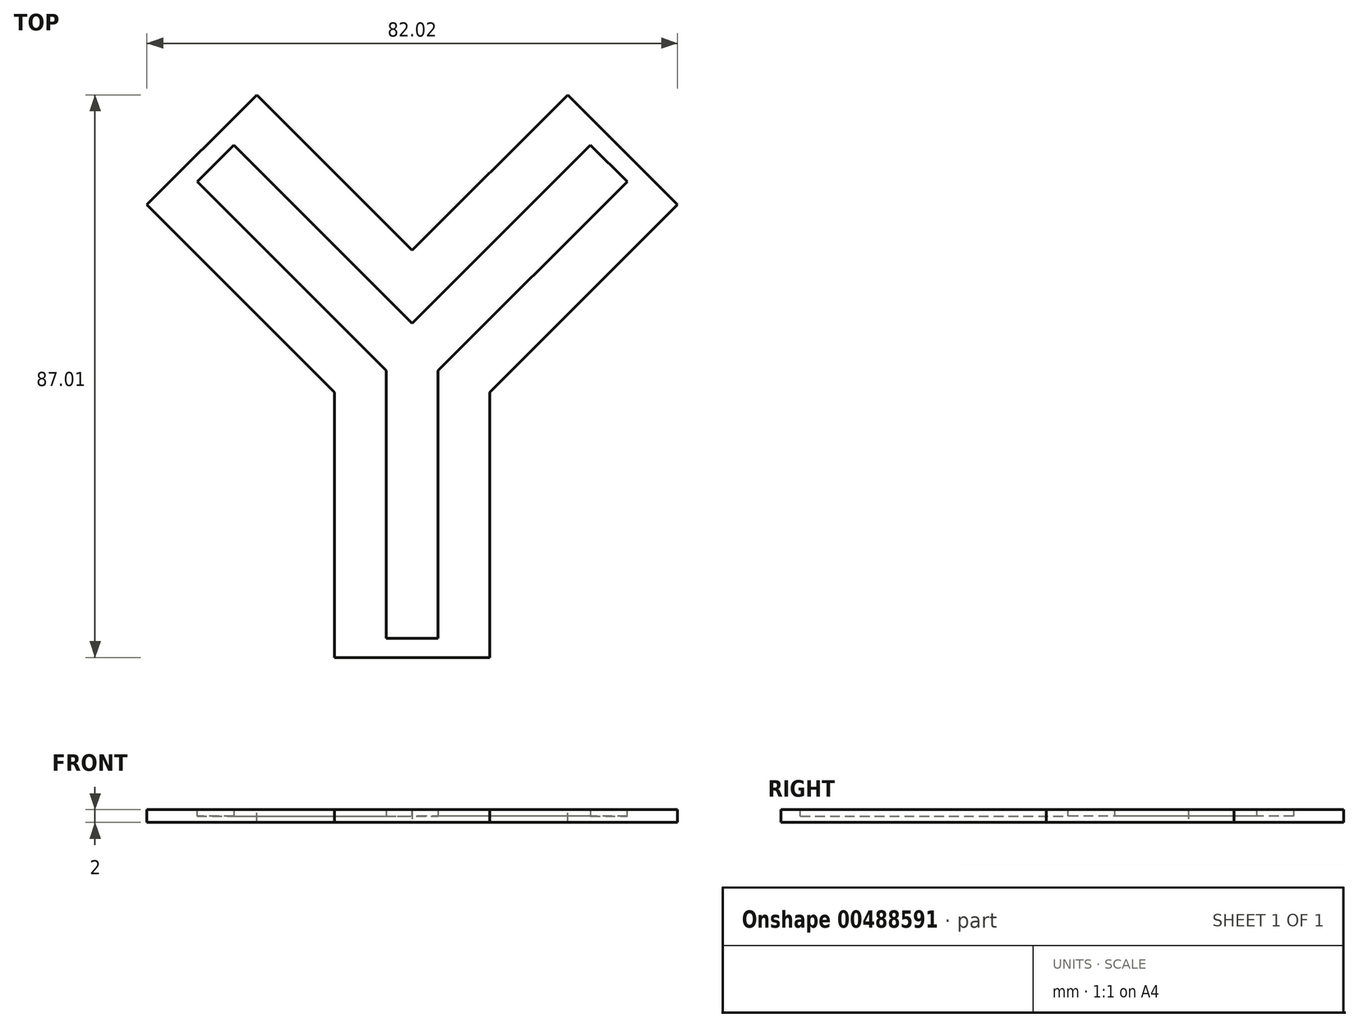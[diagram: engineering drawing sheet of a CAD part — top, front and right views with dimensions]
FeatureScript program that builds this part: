
annotation { "Feature Type Name" : "Feature", "Feature Type Description" : "" }
export const myFeature = defineFeature(function(context is Context, id is Id, definition is map)
    precondition{}
    {
        {
            var Q0;
            Q0=qCreatedBy(makeId("Front.planeOp"),FACE);
            var sketch = newSketch(context, id + "F0", { "sketchPlane" : qUnion([Q0])});
            skLineSegment(sketch, "E0", {"start": v(0, 0) * mm, "end": v(4, 0) * mm});
            skLineSegment(sketch, "E1", {"start": v(4, 0) * mm, "end": v(4, 1) * mm});
            skLineSegment(sketch, "E2", {"start": v(4, 1) * mm, "end": v(12, 1) * mm});
            skLineSegment(sketch, "E3", {"start": v(12, 1) * mm, "end": v(12, -1) * mm});
            skLineSegment(sketch, "E4", {"start": v(12, -1) * mm, "end": v(-12, -1) * mm});
            skLineSegment(sketch, "E5", {"start": v(-12, -1) * mm, "end": v(-12, 1) * mm});
            skLineSegment(sketch, "E6", {"start": v(-12, 1) * mm, "end": v(-4, 1) * mm});
            skLineSegment(sketch, "E7", {"start": v(-4, 1) * mm, "end": v(-4, 0) * mm});
            skLineSegment(sketch, "E8", {"start": v(-4, 0) * mm, "end": v(0, 0) * mm});
            skSolve(sketch);
        }
        {
            var Q0;
            Q0 = qSketchRegion(id + "F0", true);
            extrude(context, id + "F1", {"entities" : qUnion([Q0]), "depth" : 43 * mm});
        }
        {
            var Q0;
            Q0=qCreatedBy(makeId("Front.planeOp"),FACE);
            var sketch = newSketch(context, id + "F2", { "sketchPlane" : qUnion([Q0])});
            skLineSegment(sketch, "E9", {"start": v(0, 0) * mm, "end": v(0, 49.54) * mm});
            skSolve(sketch);
        }
        {
            var Q0;
            Q0=qCreatedBy(makeId("Front.planeOp"),FACE);
            var Q1;
            Q1 = qBodyType(qCreatedBy(id + "F2" ,EDGE), BodyType.WIRE);
            cPlane(context, id + "F3", {"entities" : qUnion([Q0, Q1]), "cplaneType" : CPlaneType.LINE_ANGLE, "offset" : 25 * mm, "angle" : 45 * degree, "width" : 150 * mm, "height" : 150 * mm});
        }
        {
            var Q0;
            Q0=qCreatedBy(id+"F3.planeOp",FACE);
            var Q1;
            Q1 = qBodyType(qCreatedBy(id + "F2" ,EDGE), BodyType.WIRE);
            cPlane(context, id + "F4", {"entities" : qUnion([Q0, Q1]), "cplaneType" : CPlaneType.LINE_ANGLE, "offset" : 25 * mm, "angle" : 90 * degree, "width" : 150 * mm, "height" : 150 * mm});
        }
        {
            var Q0;
            Q0=qCreatedBy(id+"F3.planeOp",FACE);
            var sketch = newSketch(context, id + "F5", { "sketchPlane" : qUnion([Q0])});
            skLineSegment(sketch, "E10", {"start": v(0, 0) * mm, "end": v(4, 0) * mm});
            skLineSegment(sketch, "E11", {"start": v(4, 0) * mm, "end": v(4, 1) * mm});
            skLineSegment(sketch, "E12", {"start": v(4, 1) * mm, "end": v(12, 1) * mm});
            skLineSegment(sketch, "E13", {"start": v(12, 1) * mm, "end": v(12, -1) * mm});
            skLineSegment(sketch, "E14", {"start": v(12, -1) * mm, "end": v(-12, -1) * mm});
            skLineSegment(sketch, "E15", {"start": v(-12, -1) * mm, "end": v(-12, 1) * mm});
            skLineSegment(sketch, "E16", {"start": v(-12, 1) * mm, "end": v(-4, 1) * mm});
            skLineSegment(sketch, "E17", {"start": v(-4, 1) * mm, "end": v(-4, 0) * mm});
            skLineSegment(sketch, "E18", {"start": v(-4, 0) * mm, "end": v(0, 0) * mm});
            skSolve(sketch);
        }
        {
            var Q0;
            Q0 = qSketchRegion(id + "F5", true);
            extrude(context, id + "F6", {"entities" : qUnion([Q0]), "operationType" : NewBodyOperationType.ADD, "depth" : 43 * mm});
        }
        {
            var Q0;
            Q0=qCreatedBy(id+"F4.planeOp",FACE);
            var sketch = newSketch(context, id + "F7", { "sketchPlane" : qUnion([Q0])});
            skLineSegment(sketch, "E19", {"start": v(0, 0) * mm, "end": v(-4, 0) * mm});
            skLineSegment(sketch, "E20", {"start": v(-4, 0) * mm, "end": v(-4, 1) * mm});
            skLineSegment(sketch, "E21", {"start": v(-4, 1) * mm, "end": v(-12, 1) * mm});
            skLineSegment(sketch, "E22", {"start": v(-12, 1) * mm, "end": v(-12, -1) * mm});
            skLineSegment(sketch, "E23", {"start": v(-12, -1) * mm, "end": v(12, -1) * mm});
            skLineSegment(sketch, "E24", {"start": v(12, -1) * mm, "end": v(12, 1) * mm});
            skLineSegment(sketch, "E25", {"start": v(12, 1) * mm, "end": v(4, 1) * mm});
            skLineSegment(sketch, "E26", {"start": v(4, 1) * mm, "end": v(4, 0) * mm});
            skLineSegment(sketch, "E27", {"start": v(4, 0) * mm, "end": v(0, 0) * mm});
            skSolve(sketch);
        }
        {
            var Q0;
            Q0 = qSketchRegion(id + "F7", true);
            extrude(context, id + "F8", {"entities" : qUnion([Q0]), "operationType" : NewBodyOperationType.ADD, "depth" : 43 * mm});
        }
        {
            var Q0;
            Q0=makeQuery(id+"F1.opExtrude","CAP_FACE",FACE,{"disambiguationData":[OSD([sQuery(id+"F0.wireOp",EDGE,"E0"),sQuery(id+"F0.wireOp",EDGE,"E1"),sQuery(id+"F0.wireOp",EDGE,"E2"),sQuery(id+"F0.wireOp",EDGE,"E3"),sQuery(id+"F0.wireOp",EDGE,"E4"),sQuery(id+"F0.wireOp",EDGE,"E5"),sQuery(id+"F0.wireOp",EDGE,"E6"),sQuery(id+"F0.wireOp",EDGE,"E7"),sQuery(id+"F0.wireOp",EDGE,"E8")])],"isStart":false});
            var sketch = newSketch(context, id + "F9", { "sketchPlane" : qUnion([Q0])});
            skLineSegment(sketch, "E28", {"start": v(0, 0) * mm, "end": v(-4, 0) * mm});
            skLineSegment(sketch, "E29", {"start": v(-4, 0) * mm, "end": v(-4, 1) * mm});
            skLineSegment(sketch, "E30", {"start": v(-4, 1) * mm, "end": v(4, 1) * mm});
            skLineSegment(sketch, "E31", {"start": v(4, 1) * mm, "end": v(4, 0) * mm});
            skLineSegment(sketch, "E32", {"start": v(4, 0) * mm, "end": v(0, 0) * mm});
            skSolve(sketch);
        }
        {
            var Q0;
            Q0 = qSketchRegion(id + "F9", true);
            extrude(context, id + "F10", {"entities" : qUnion([Q0]), "operationType" : NewBodyOperationType.REMOVE, "oppositeDirection" : true, "depth" : 43 * mm});
        }
        {
            var Q0;
            Q0=makeQuery(id+"F6.opExtrude","CAP_FACE",FACE,{"disambiguationData":[OSD([sQuery(id+"F5.wireOp",EDGE,"E10"),sQuery(id+"F5.wireOp",EDGE,"E11"),sQuery(id+"F5.wireOp",EDGE,"E12"),sQuery(id+"F5.wireOp",EDGE,"E13"),sQuery(id+"F5.wireOp",EDGE,"E14"),sQuery(id+"F5.wireOp",EDGE,"E15"),sQuery(id+"F5.wireOp",EDGE,"E16"),sQuery(id+"F5.wireOp",EDGE,"E17"),sQuery(id+"F5.wireOp",EDGE,"E18")])],"isStart":false});
            var sketch = newSketch(context, id + "F11", { "sketchPlane" : qUnion([Q0])});
            skLineSegment(sketch, "E33", {"start": v(0, 0) * mm, "end": v(-4, 0) * mm});
            skLineSegment(sketch, "E34", {"start": v(-4, 0) * mm, "end": v(-4, 1) * mm});
            skLineSegment(sketch, "E35", {"start": v(-4, 1) * mm, "end": v(4, 1) * mm});
            skLineSegment(sketch, "E36", {"start": v(4, 1) * mm, "end": v(4, 0) * mm});
            skLineSegment(sketch, "E37", {"start": v(4, 0) * mm, "end": v(0, 0) * mm});
            skSolve(sketch);
        }
        {
            var Q0;
            Q0 = qSketchRegion(id + "F11", true);
            extrude(context, id + "F12", {"entities" : qUnion([Q0]), "operationType" : NewBodyOperationType.REMOVE, "oppositeDirection" : true, "depth" : 43 * mm});
        }
        {
            var Q0;
            Q0=makeQuery(id+"F8.opExtrude","CAP_FACE",FACE,{"disambiguationData":[OSD([sQuery(id+"F7.wireOp",EDGE,"E19"),sQuery(id+"F7.wireOp",EDGE,"E20"),sQuery(id+"F7.wireOp",EDGE,"E21"),sQuery(id+"F7.wireOp",EDGE,"E22"),sQuery(id+"F7.wireOp",EDGE,"E23"),sQuery(id+"F7.wireOp",EDGE,"E24"),sQuery(id+"F7.wireOp",EDGE,"E25"),sQuery(id+"F7.wireOp",EDGE,"E26"),sQuery(id+"F7.wireOp",EDGE,"E27")])],"isStart":false});
            var sketch = newSketch(context, id + "F13", { "sketchPlane" : qUnion([Q0])});
            skLineSegment(sketch, "E38", {"start": v(0, 0) * mm, "end": v(-4, 0) * mm});
            skLineSegment(sketch, "E39", {"start": v(-4, 0) * mm, "end": v(-4, 1) * mm});
            skLineSegment(sketch, "E40", {"start": v(-4, 1) * mm, "end": v(4, 1) * mm});
            skLineSegment(sketch, "E41", {"start": v(4, 1) * mm, "end": v(4, 0) * mm});
            skLineSegment(sketch, "E42", {"start": v(4, 0) * mm, "end": v(0, 0) * mm});
            skSolve(sketch);
        }
        {
            var Q0;
            Q0 = qSketchRegion(id + "F13", true);
            extrude(context, id + "F14", {"entities" : qUnion([Q0]), "operationType" : NewBodyOperationType.REMOVE, "oppositeDirection" : true, "depth" : 43 * mm});
        }
        {
            var Q0;
            Q0=makeQuery(id+"F1.opExtrude","CAP_FACE",FACE,{"disambiguationData":[OSD([sQuery(id+"F0.wireOp",EDGE,"E0"),sQuery(id+"F0.wireOp",EDGE,"E1"),sQuery(id+"F0.wireOp",EDGE,"E2"),sQuery(id+"F0.wireOp",EDGE,"E3"),sQuery(id+"F0.wireOp",EDGE,"E4"),sQuery(id+"F0.wireOp",EDGE,"E5"),sQuery(id+"F0.wireOp",EDGE,"E6"),sQuery(id+"F0.wireOp",EDGE,"E7"),sQuery(id+"F0.wireOp",EDGE,"E8")])],"isStart":false});
            var sketch = newSketch(context, id + "F15", { "sketchPlane" : qUnion([Q0])});
            skLineSegment(sketch, "E43.bottom", {"start": v(-12, 1) * mm, "end": v(12, 1) * mm});
            skLineSegment(sketch, "E43.top", {"start": v(-12, -1) * mm, "end": v(12, -1) * mm});
            skLineSegment(sketch, "E43.left", {"start": v(-12, 1) * mm, "end": v(-12, -1) * mm});
            skLineSegment(sketch, "E43.right", {"start": v(12, 1) * mm, "end": v(12, -1) * mm});
            skPoint(sketch, "E43.middle", {"position": v(0, 0) * mm});
            skSolve(sketch);
        }
        {
            var Q0;
            Q0 = qSketchRegion(id + "F15", true);
            extrude(context, id + "F16", {"entities" : qUnion([Q0]), "operationType" : NewBodyOperationType.ADD, "depth" : 3 * mm});
        }
        {
            var Q0;
            Q0=makeQuery(id+"F6.opExtrude","CAP_FACE",FACE,{"disambiguationData":[OSD([sQuery(id+"F5.wireOp",EDGE,"E10"),sQuery(id+"F5.wireOp",EDGE,"E11"),sQuery(id+"F5.wireOp",EDGE,"E12"),sQuery(id+"F5.wireOp",EDGE,"E13"),sQuery(id+"F5.wireOp",EDGE,"E14"),sQuery(id+"F5.wireOp",EDGE,"E15"),sQuery(id+"F5.wireOp",EDGE,"E16"),sQuery(id+"F5.wireOp",EDGE,"E17"),sQuery(id+"F5.wireOp",EDGE,"E18")])],"isStart":false});
            var sketch = newSketch(context, id + "F17", { "sketchPlane" : qUnion([Q0])});
            skLineSegment(sketch, "E44.bottom", {"start": v(-12, 1) * mm, "end": v(12, 1) * mm});
            skLineSegment(sketch, "E44.top", {"start": v(-12, -1) * mm, "end": v(12, -1) * mm});
            skLineSegment(sketch, "E44.left", {"start": v(-12, 1) * mm, "end": v(-12, -1) * mm});
            skLineSegment(sketch, "E44.right", {"start": v(12, 1) * mm, "end": v(12, -1) * mm});
            skPoint(sketch, "E44.middle", {"position": v(0, 0) * mm});
            skSolve(sketch);
        }
        {
            var Q0;
            Q0 = qSketchRegion(id + "F17", true);
            extrude(context, id + "F18", {"entities" : qUnion([Q0]), "operationType" : NewBodyOperationType.ADD, "depth" : 3 * mm});
        }
        {
            var Q0;
            Q0=makeQuery(id+"F8.opExtrude","CAP_FACE",FACE,{"disambiguationData":[OSD([sQuery(id+"F7.wireOp",EDGE,"E19"),sQuery(id+"F7.wireOp",EDGE,"E20"),sQuery(id+"F7.wireOp",EDGE,"E21"),sQuery(id+"F7.wireOp",EDGE,"E22"),sQuery(id+"F7.wireOp",EDGE,"E23"),sQuery(id+"F7.wireOp",EDGE,"E24"),sQuery(id+"F7.wireOp",EDGE,"E25"),sQuery(id+"F7.wireOp",EDGE,"E26"),sQuery(id+"F7.wireOp",EDGE,"E27")])],"isStart":false});
            var sketch = newSketch(context, id + "F19", { "sketchPlane" : qUnion([Q0])});
            skLineSegment(sketch, "E45.bottom", {"start": v(-12, 1) * mm, "end": v(12, 1) * mm});
            skLineSegment(sketch, "E45.top", {"start": v(-12, -1) * mm, "end": v(12, -1) * mm});
            skLineSegment(sketch, "E45.left", {"start": v(-12, 1) * mm, "end": v(-12, -1) * mm});
            skLineSegment(sketch, "E45.right", {"start": v(12, 1) * mm, "end": v(12, -1) * mm});
            skPoint(sketch, "E45.middle", {"position": v(0, 0) * mm});
            skSolve(sketch);
        }
        {
            var Q0;
            Q0 = qSketchRegion(id + "F19", true);
            extrude(context, id + "F20", {"entities" : qUnion([Q0]), "operationType" : NewBodyOperationType.ADD, "depth" : 3 * mm});
        }
    });
